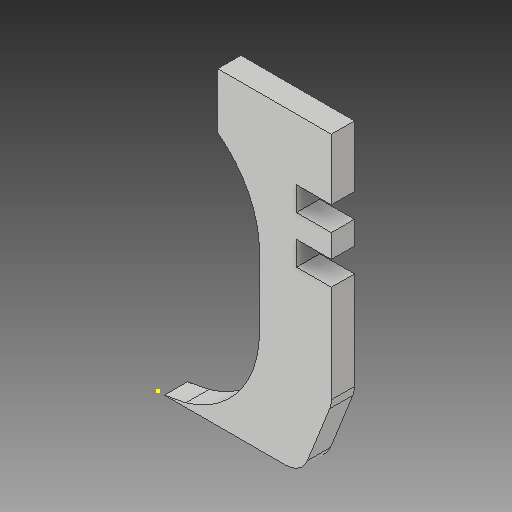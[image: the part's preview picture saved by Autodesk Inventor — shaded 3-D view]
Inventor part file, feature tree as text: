
AUTODESK INVENTOR PART (.ipt)
format: ipt  version: 2017 (Build 210142000, 142)  size: 116,224 bytes
history: native  units: in
note: dims shown in document units (in); Inventor stores cm internally (conversion verified against a paired STEP export)
features: sketch x4, other x3
ambient origin geometry x8: Origin, YZ Plane, XZ Plane, XY Plane, X Axis, Y Axis, Z Axis, Center Point
bodies: Solid1 (feature_tree)
feature tree (7):
  other  "Finger.ipt"
  other  "Solid1::Finger.ipt"
  other  "TaggingFeature1"
  sketch  "Sketch1"  dims[d0=0.3937in]
  sketch  "Sketch2"
  sketch  "Sketch3"
  sketch  "Sketch4"
